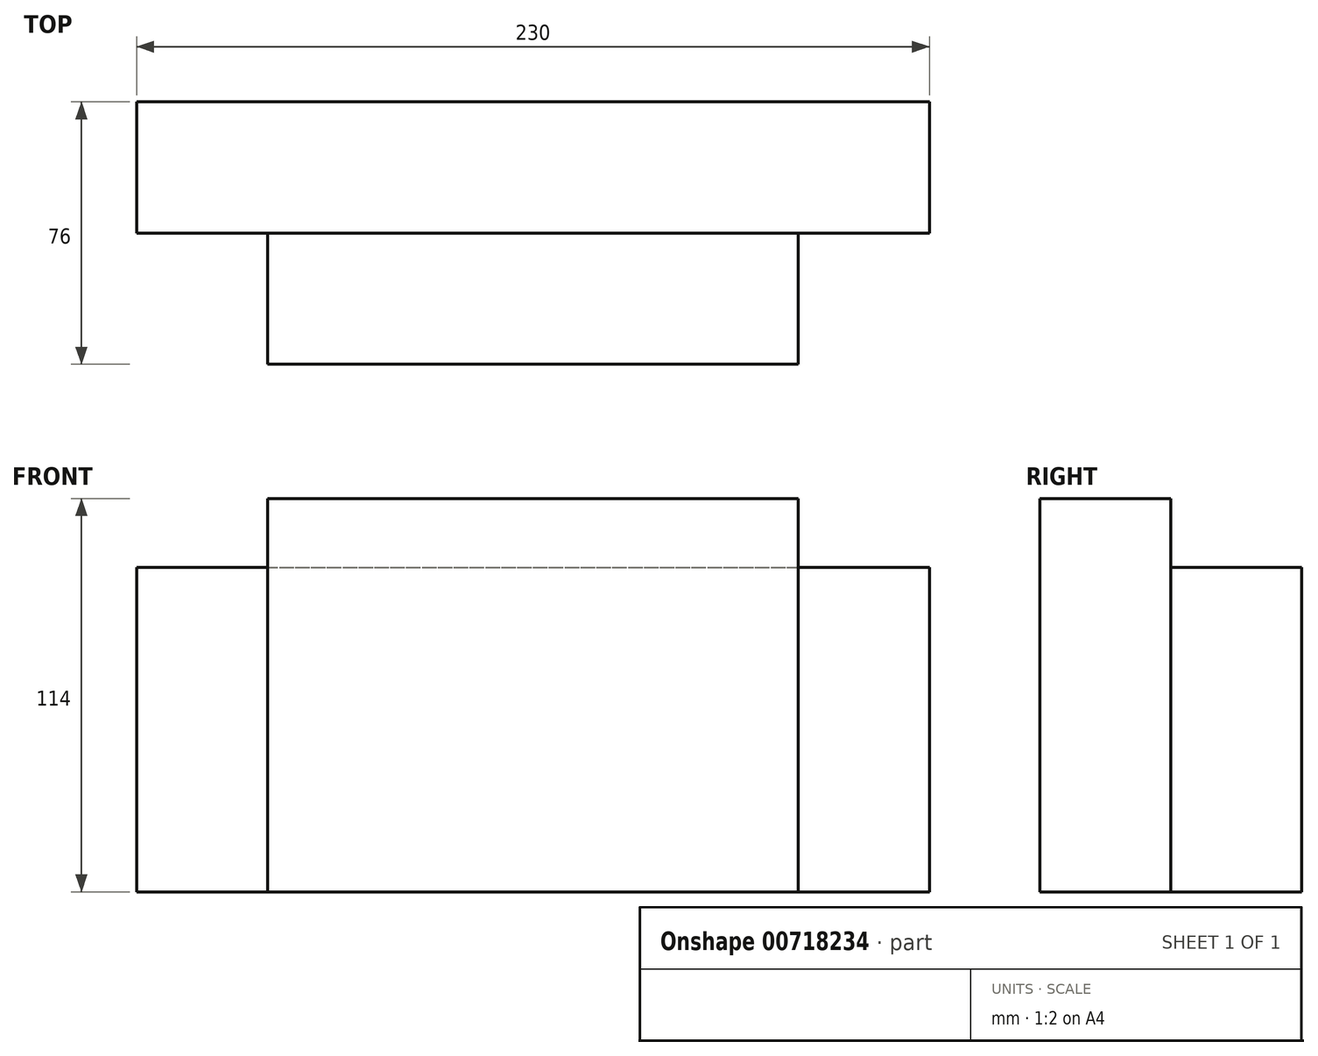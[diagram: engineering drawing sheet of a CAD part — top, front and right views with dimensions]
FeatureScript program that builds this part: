
annotation { "Feature Type Name" : "Feature", "Feature Type Description" : "" }
export const myFeature = defineFeature(function(context is Context, id is Id, definition is map)
    precondition{}
    {
        {
            var Q0;
            Q0=qCreatedBy(makeId("Front.planeOp"),FACE);
            var sketch = newSketch(context, id + "F0", { "sketchPlane" : qUnion([Q0])});
            skLineSegment(sketch, "E0.bottom", {"start": v(115, -57) * mm, "end": v(-115, -57) * mm});
            skLineSegment(sketch, "E0.top", {"start": v(115, 57) * mm, "end": v(-115, 57) * mm});
            skLineSegment(sketch, "E0.left", {"start": v(115, -57) * mm, "end": v(115, 57) * mm});
            skLineSegment(sketch, "E0.right", {"start": v(-115, -57) * mm, "end": v(-115, 57) * mm});
            skPoint(sketch, "E0.middle", {"position": v(0, 0) * mm});
            skSolve(sketch);
        }
        {
            var Q0;
            Q0=makeQuery(id+"F0.imprint","IMPRINT",FACE,{"disambiguationData":[TD([[makeQuery(id+"F0.imprint","IMPRINT",EDGE,{"derivedFrom":sQuery(id+"F0.wireOp",EDGE,"E0.bottom")}),-1.0]])]});
            extrude(context, id + "F1", {"entities" : qUnion([Q0]), "depth" : 76 * mm, "offsetDistance" : 25 * mm});
        }
        {
            var Q0;
            Q0=qCreatedBy(makeId("Right.planeOp"),FACE);
            cPlane(context, id + "F2", {"entities" : qUnion([Q0]), "cplaneType" : CPlaneType.OFFSET, "offset" : 115 * mm, "width" : 150 * mm, "height" : 150 * mm});
        }
        {
            var Q0;
            Q0=qCreatedBy(id+"F2.planeOp",FACE);
            var sketch = newSketch(context, id + "F3", { "sketchPlane" : qUnion([Q0])});
            skLineSegment(sketch, "E1.bottom", {"start": v(0, 57) * mm, "end": v(-38, 57) * mm});
            skLineSegment(sketch, "E1.top", {"start": v(0, 37) * mm, "end": v(-38, 37) * mm});
            skLineSegment(sketch, "E1.left", {"start": v(0, 57) * mm, "end": v(0, 37) * mm});
            skLineSegment(sketch, "E1.right", {"start": v(-38, 57) * mm, "end": v(-38, 37) * mm});
            skSolve(sketch);
        }
        {
            var Q0;
            Q0=makeQuery(id+"F3.imprint","IMPRINT",FACE,{"disambiguationData":[TD([[makeQuery(id+"F3.imprint","IMPRINT",EDGE,{"derivedFrom":sQuery(id+"F3.wireOp",EDGE,"E1.bottom")}),1.0]])]});
            extrude(context, id + "F4", {"entities" : qUnion([Q0]), "operationType" : NewBodyOperationType.REMOVE, "endBound" : BoundingType.THROUGH_ALL, "oppositeDirection" : true, "depth" : 25 * mm, "offsetDistance" : 25 * mm});
        }
        {
            var Q0;
            Q0=qCreatedBy(makeId("Top.planeOp"),FACE);
            cPlane(context, id + "F5", {"entities" : qUnion([Q0]), "cplaneType" : CPlaneType.OFFSET, "offset" : 57 * mm, "width" : 150 * mm, "height" : 150 * mm});
        }
        {
            var Q0;
            Q0=qCreatedBy(id+"F5.planeOp",FACE);
            var sketch = newSketch(context, id + "F6", { "sketchPlane" : qUnion([Q0])});
            skLineSegment(sketch, "E2.bottom", {"start": v(-115, -76) * mm, "end": v(-77, -76) * mm});
            skLineSegment(sketch, "E2.top", {"start": v(-115, -38) * mm, "end": v(-77, -38) * mm});
            skLineSegment(sketch, "E2.left", {"start": v(-115, -76) * mm, "end": v(-115, -38) * mm});
            skLineSegment(sketch, "E2.right", {"start": v(-77, -76) * mm, "end": v(-77, -38) * mm});
            skLineSegment(sketch, "E3.bottom", {"start": v(115, -76) * mm, "end": v(77, -76) * mm});
            skLineSegment(sketch, "E3.top", {"start": v(115, -38) * mm, "end": v(77, -38) * mm});
            skLineSegment(sketch, "E3.left", {"start": v(115, -76) * mm, "end": v(115, -38) * mm});
            skLineSegment(sketch, "E3.right", {"start": v(77, -76) * mm, "end": v(77, -38) * mm});
            skSolve(sketch);
        }
        {
            var Q0;
            Q0=makeQuery(id+"F6.imprint","IMPRINT",FACE,{"disambiguationData":[TD([[makeQuery(id+"F6.imprint","IMPRINT",EDGE,{"derivedFrom":sQuery(id+"F6.wireOp",EDGE,"E2.bottom")}),1.0]])]});
            var Q1;
            Q1=makeQuery(id+"F6.imprint","IMPRINT",FACE,{"disambiguationData":[TD([[makeQuery(id+"F6.imprint","IMPRINT",EDGE,{"derivedFrom":sQuery(id+"F6.wireOp",EDGE,"E3.bottom")}),-1.0]])]});
            extrude(context, id + "F7", {"entities" : qUnion([Q0, Q1]), "operationType" : NewBodyOperationType.REMOVE, "endBound" : BoundingType.THROUGH_ALL, "oppositeDirection" : true, "depth" : 25 * mm, "offsetDistance" : 25 * mm});
        }
    });
